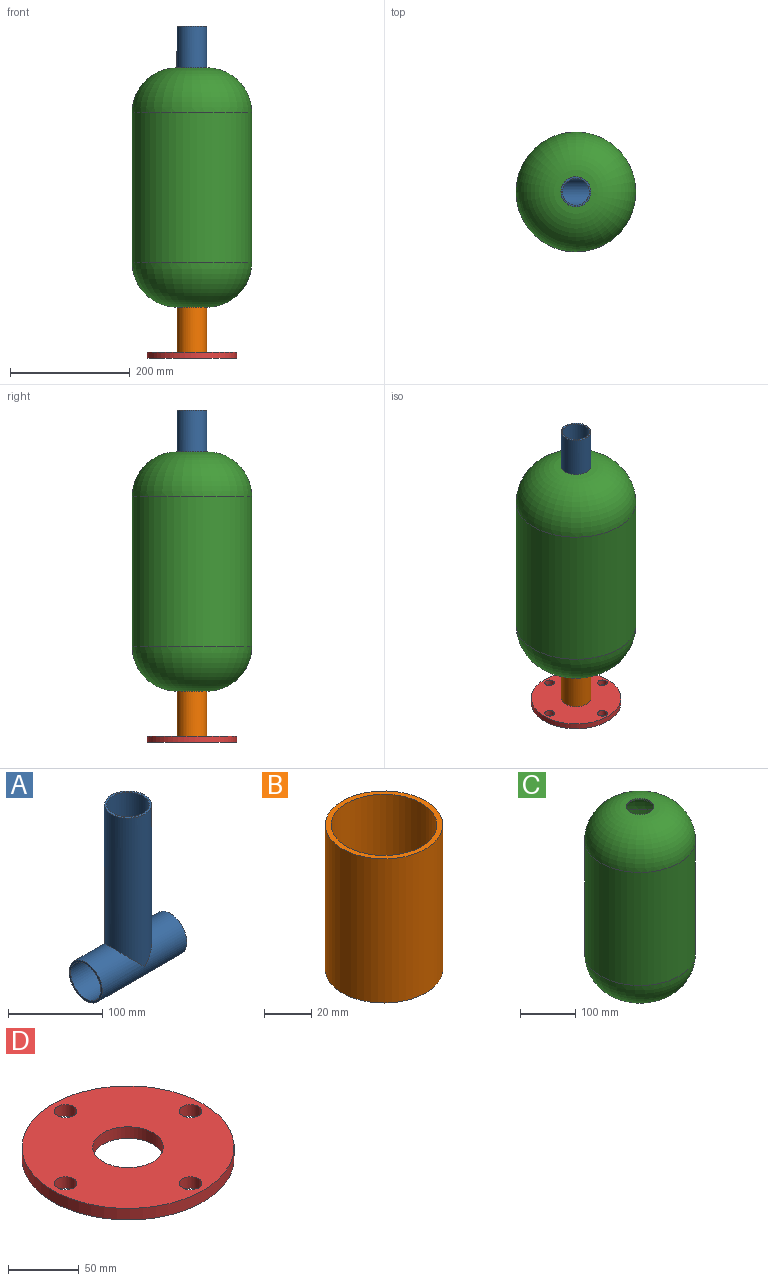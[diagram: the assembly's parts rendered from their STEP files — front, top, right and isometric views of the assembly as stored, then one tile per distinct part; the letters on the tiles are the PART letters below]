
ASSEMBLY  parts=4 mates=3
PART A: 7 faces, bbox 127x50x223.4 mm
  f0: cylinder r=25mm len=127mm, axis (-1,0,0), area 17449.1mm2, adj f1,f2,f3
  f1: plane 50x50mm, normal (1,0,0), area 373.1mm2, adj f0,f5
  f2: plane 50x50mm, normal (-1,0,0), area 373.1mm2, adj f0,f5
  f3: cylinder r=25mm len=198.43mm, axis (0,0,-1), area 28669.5mm2, adj f0,f6
  f4: cylinder r=22.5mm len=198.43mm, axis (0,0,-1), area 26027.5mm2, adj f5,f6
  f5: cylinder r=22.5mm len=127mm, axis (-1,0,0), area 15929.2mm2, adj f1,f2,f4
  f6: plane 50x50mm, normal (0,0,1), area 373.1mm2, adj f3,f4
PART B: 4 faces, bbox 50x50x75 mm
  f0: cylinder r=25mm len=75mm, axis (0,0,-1), area 11781mm2, adj f1,f2
  f1: plane 50x50mm, normal (0,0,1), area 373.1mm2, adj f0,f3
  f2: plane 50x50mm, normal (0,0,-1), area 373.1mm2, adj f0,f3
  f3: cylinder r=22.5mm len=75mm, axis (0,0,-1), area 10602.9mm2, adj f1,f2
PART C: 8 faces, bbox 200x200x400 mm
  f0: cylinder r=25mm len=50mm, axis (0,0,-1), area 392.7mm2, adj f2,f6
  f1: cylinder r=100mm len=250mm, axis (0,0,-1), area 157079.6mm2, adj f2,f3
  f2: torus R=25mm, axis (0,0,1), area 53848.4mm2, adj f0,f1
  f3: torus R=25mm, axis (0,0,1), area 53848.4mm2, adj f1,f4
  f4: cylinder r=25mm len=50mm, axis (0,0,-1), area 392.7mm2, adj f3,f7
  f5: cylinder r=97.5mm len=250mm, axis (0,0,-1), area 153152.6mm2, adj f6,f7
  f6: torus R=25mm, axis (0,0,1), area 50914.7mm2, adj f0,f5
  f7: torus R=25mm, axis (0,0,1), area 50914.7mm2, adj f4,f5
PART D: 8 faces, bbox 150x150x10 mm
  f0: cylinder r=8mm len=16mm, axis (0,0,-1), area 502.7mm2, adj f6,f7
  f1: cylinder r=8mm len=16mm, axis (0,0,-1), area 502.7mm2, adj f6,f7
  f2: cylinder r=8mm len=16mm, axis (0,0,-1), area 502.7mm2, adj f6,f7
  f3: cylinder r=8mm len=16mm, axis (0,0,-1), area 502.7mm2, adj f6,f7
  f4: cylinder r=25mm len=50mm, axis (0,0,-1), area 1570.8mm2, adj f6,f7
  f5: cylinder r=75mm len=150mm, axis (0,0,-1), area 4712.4mm2, adj f6,f7
  f6: plane 150x150mm, normal (0,0,1), area 14903.7mm2, adj f0,f1,f2,f3,f4,f5
  f7: plane 150x150mm, normal (0,0,-1), area 14903.7mm2, adj f0,f1,f2,f3,f4,f5
PLACE A rot(axis=(0,0,1),0deg) t=(0,0,397.78)mm
PLACE B t=(0,0,51.21)mm
PLACE C rot(axis=(0,0,1),0deg) t=(0,0,126.21)mm
PLACE D t=(0,0,41.21)mm
MATE pin_slot B.f0 <-> C.f0  axis (0,0,-1) through (0,0,126.21)mm
MATE slider A.f3 <-> C.f0  axis (0,0,-1) through (0,0,496.4)mm
MATE pin_slot D.f5 <-> B.f0  axis (0,0,1) through (0,0,51.21)mm
